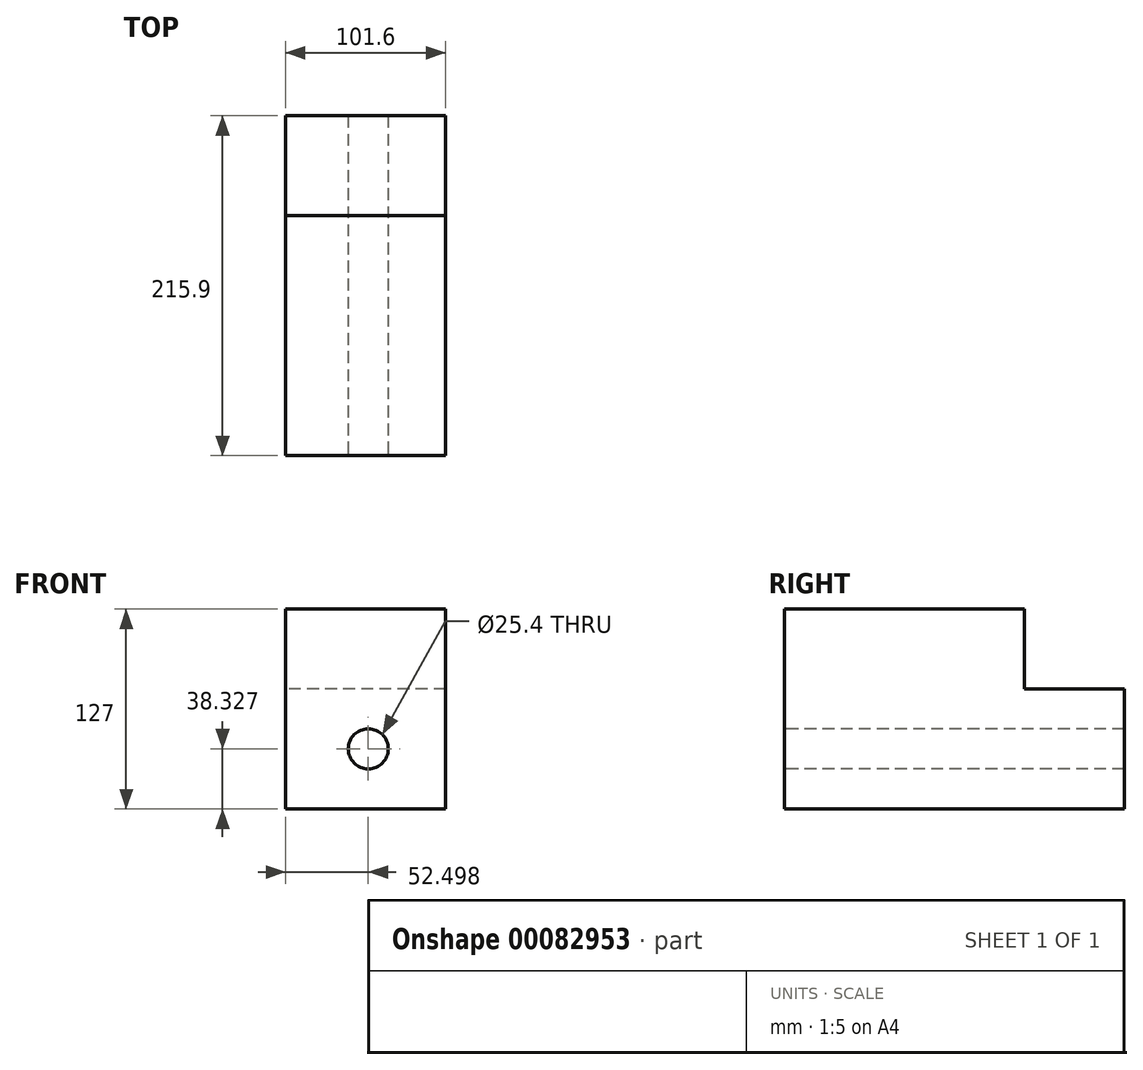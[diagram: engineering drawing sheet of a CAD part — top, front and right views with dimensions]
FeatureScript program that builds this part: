
annotation { "Feature Type Name" : "Feature", "Feature Type Description" : "" }
export const myFeature = defineFeature(function(context is Context, id is Id, definition is map)
    precondition{}
    {
        {
            var Q0;
            Q0=qCreatedBy(makeId("Top.planeOp"),FACE);
            var sketch = newSketch(context, id + "F0", { "sketchPlane" : qUnion([Q0])});
            skLineSegment(sketch, "E0.bottom", {"start": v(-57.46, 121.87) * mm, "end": v(44.14, 121.87) * mm});
            skLineSegment(sketch, "E0.top", {"start": v(-57.46, -30.53) * mm, "end": v(44.14, -30.53) * mm});
            skLineSegment(sketch, "E0.left", {"start": v(-57.46, 121.87) * mm, "end": v(-57.46, -30.53) * mm});
            skLineSegment(sketch, "E0.right", {"start": v(44.14, 121.87) * mm, "end": v(44.14, -30.53) * mm});
            skSolve(sketch);
        }
        {
            var Q0;
            Q0=makeQuery(id+"F0.imprint","IMPRINT",FACE,{"disambiguationData":[TD([[makeQuery(id+"F0.imprint","IMPRINT",EDGE,{"derivedFrom":sQuery(id+"F0.wireOp",EDGE,"E0.bottom")}),-1.0]])]});
            extrude(context, id + "F1", {"entities" : qUnion([Q0]), "depth" : 127 * mm});
        }
        {
            var Q0;
            Q0=makeQuery(id+"F1.opExtrude","SWEPT_FACE",FACE,{"disambiguationData":[OSD([sQuery(id+"F0.wireOp",EDGE,"E0.top")])]});
            var sketch = newSketch(context, id + "F2", { "sketchPlane" : qUnion([Q0])});
            skSolve(sketch);
        }
        {
            var Q0;
            {var subQ0=sQuery(id+"F0.wireOp",EDGE,"E0.top");Q0=makeQuery(id+"F2.imprint","IMPRINT",FACE,{"disambiguationData":[TD([[makeQuery(id+"F2.imprint","IMPRINT",EDGE,{"derivedFrom":makeQuery(id+"F1.opExtrude","CAP_EDGE",EDGE,{"disambiguationData":[OSD([subQ0])],"isStart":true})}),1.0]])]});}
            var sketch = newSketch(context, id + "F3", { "sketchPlane" : qUnion([Q0])});
            skLineSegment(sketch, "E1", {"start": v(-55.48, 0) * mm, "end": v(-55.48, 38.1) * mm});
            skLineSegment(sketch, "E2", {"start": v(-55.48, 0) * mm, "end": v(-4.68, 0) * mm});
            skCircle(sketch, "E3", {"center": v(-4.96, 38.33) * mm, "radius": 11.78 * mm});
            skSolve(sketch);
        }
        {
            var Q0;
            Q0=makeQuery(id+"F1.opExtrude","SWEPT_FACE",FACE,{"disambiguationData":[OSD([sQuery(id+"F0.wireOp",EDGE,"E0.bottom")])]});
            var sketch = newSketch(context, id + "F4", { "sketchPlane" : qUnion([Q0])});
            skLineSegment(sketch, "E4.bottom", {"start": v(-44.14, 0) * mm, "end": v(57.46, 0) * mm});
            skLineSegment(sketch, "E4.top", {"start": v(-44.14, 76.2) * mm, "end": v(57.46, 76.2) * mm});
            skLineSegment(sketch, "E4.left", {"start": v(-44.14, 0) * mm, "end": v(-44.14, 76.2) * mm});
            skLineSegment(sketch, "E4.right", {"start": v(57.46, 0) * mm, "end": v(57.46, 76.2) * mm});
            skSolve(sketch);
        }
        {
            var Q0;
            Q0 = qSketchRegion(id + "F4", true);
            extrude(context, id + "F5", {"entities" : qUnion([Q0]), "operationType" : NewBodyOperationType.ADD, "depth" : 63.5 * mm});
        }
        {
            var Q0;
            Q0=sQuery(id+"F3.wireOp",VERTEX,"E3.center");
            var Q1;
            Q1=makeQuery(id+"F1.opExtrude","SWEPT_BODY",BODY,{"disambiguationData":[OSD([sQuery(id+"F0.wireOp",EDGE,"E0.bottom"),sQuery(id+"F0.wireOp",EDGE,"E0.top"),sQuery(id+"F0.wireOp",EDGE,"E0.left"),sQuery(id+"F0.wireOp",EDGE,"E0.right")])]});
            hole(context, id + "F6", {"style" : HoleStyle.SIMPLE, "endStyle" : HoleEndStyle.THROUGH, "holeDiameter" : 25.4 * mm, "locations" : qUnion([Q0]), "scope" : qUnion([Q1]), "isTappedThrough" : true});
        }
    });
